# Revit family: Faucet-Pull_Down-American_Standard-Edgewater-4932.300
name_source: partatom
category: Plumbing Fixtures
revit_build: Autodesk Revit 2014 (Build: 20130308_1515(x64)
units: mm (PartAtom-declared; Revit-internal decimal feet)

## types (1)
- 4932.300
    ADA Compliant = Yes
    Assembly Code = D2020300
    CW Connection = Yes
    CWFU = 1.5
    Cold Water Connection Diameter = 3/8"
    Default Elevation = 0"
    Description = Edgewater Pull-Down Kitchen Faucet with Selectflo.
    HW Connection = Yes
    HWFU = 1.5
    Height = 17 7/16"
    Hot Water Connection Diameter = 3/8"
    Length = 9"
    Manufacturer = American Standard
    Material = Metal-American Standard-002-Polished Chrome
    Model = 4932.300
    Product Documentation Link = https://www.americanstandard-us.com
    Product URL = https://www.americanstandard-us.com
    Revised Date = 02/09/2017
    Specification = High arc brass spout with pull-down SelectFlo™ 4 function spray head with pause feature. Metal body and 2 part ADA metal lever handle. Toggle down into spray mode and rotate dial to select desired spray. Washerless 35 mm ceramic disc valve cartridge.
    URL = http://www.americanstandard-us.com
    Vent Connection = No
    WFU = 0
    Waste Connection = No

## geometry (parser evidence)
native form markers: Sweep x1
no freeform markers — native parametric forms only
